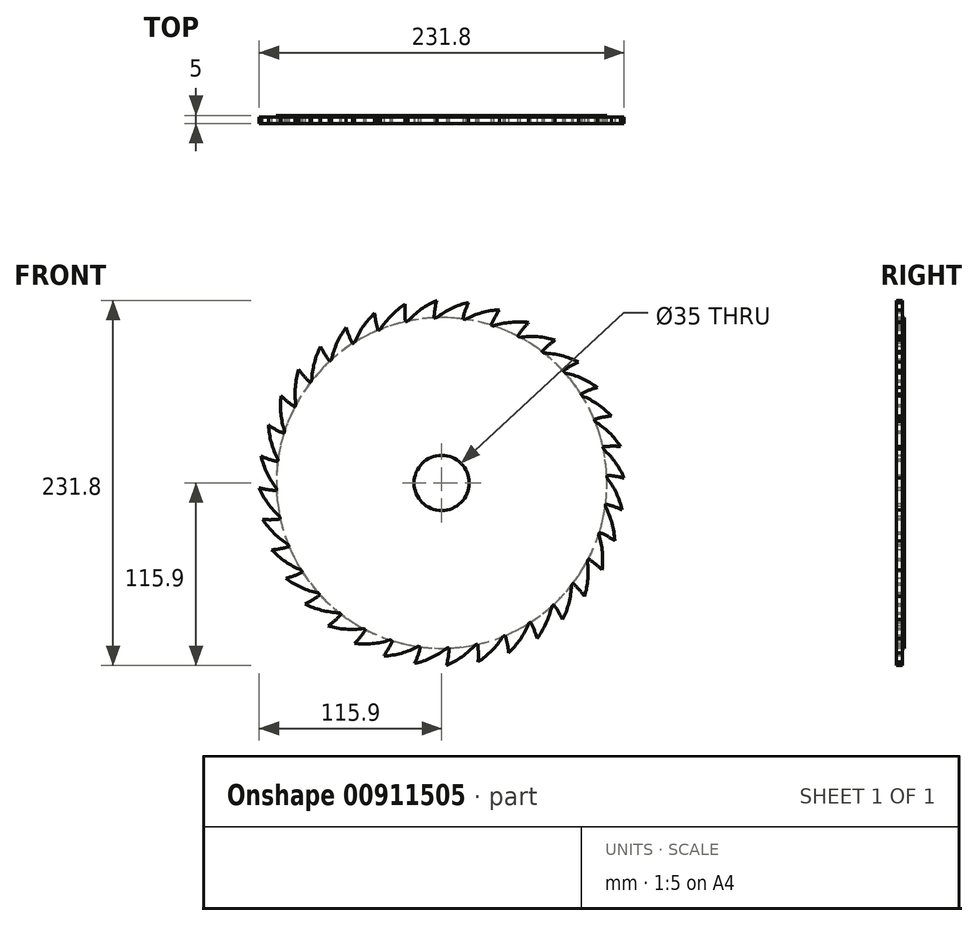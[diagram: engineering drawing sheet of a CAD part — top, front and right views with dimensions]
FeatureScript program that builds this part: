
annotation { "Feature Type Name" : "Feature", "Feature Type Description" : "" }
export const myFeature = defineFeature(function(context is Context, id is Id, definition is map)
    precondition{}
    {
        {
            var Q0;
            Q0=qCreatedBy(makeId("Front.planeOp"),FACE);
            var sketch = newSketch(context, id + "F0", { "sketchPlane" : qUnion([Q0])});
            skCircle(sketch, "E0", {"center": v(0, 0) * mm, "radius": 125 * mm});
            skCircle(sketch, "E1", {"center": v(0, 0) * mm, "radius": 105 * mm});
            skSolve(sketch);
        }
        {
            var Q0;
            Q0=makeQuery(id+"F0.imprint","IMPRINT",FACE,{"disambiguationData":[TD([[makeQuery(id+"F0.imprint","IMPRINT",EDGE,{"derivedFrom":sQuery(id+"F0.wireOp",EDGE,"E1")}),1.0]])]});
            extrude(context, id + "F1", {"entities" : qUnion([Q0]), "endBound" : BoundingType.SYMMETRIC, "depth" : 5 * mm, "offsetDistance" : 25 * mm});
        }
        {
            var Q0;
            Q0=makeQuery(id+"F1.opExtrude","CAP_FACE",FACE,{"disambiguationData":[OSD([sQuery(id+"F0.wireOp",EDGE,"E1")])],"isStart":false});
            var sketch = newSketch(context, id + "F2", { "sketchPlane" : qUnion([Q0])});
            skLineSegment(sketch, "E2", {"start": v(4.66, 77.54) * mm, "end": v(40.5, 61.1) * mm});
            skArc(sketch, "E3", {"start": v(55.27, 101.92) * mm, "mid": v(26.4, 97.15) * mm, "end": v(4.66, 77.54) * mm});
            skArc(sketch, "E4", {"start": v(55.27, 101.92) * mm, "mid": v(43.34, 83.16) * mm, "end": v(40.5, 61.1) * mm});
            skSolve(sketch);
        }
        {
            var Q0;
            {var subQ0=sQuery(id+"F2.wireOp",EDGE,"E4");var subQ1=sQuery(id+"F2.wireOp",EDGE,"E3");var subQ2=makeQuery(id+"F2.imprint","INTERSECT",VERTEX,{"derivedFrom":[subQ1,subQ0]});Q0=makeQuery(id+"F2.imprint","IMPRINT",FACE,{"disambiguationData":[TD([[makeQuery(id+"F2.imprint","IMPRINT",EDGE,{"disambiguationData":[TD([[subQ2,-1.0]])],"derivedFrom":subQ1}),1.0]])]});}
            var Q1;
            Q1=makeQuery(id+"F1.opExtrude","CAP_FACE",FACE,{"disambiguationData":[OSD([sQuery(id+"F0.wireOp",EDGE,"E1")])],"isStart":true});
            extrude(context, id + "F3", {"entities" : qUnion([Q0]), "operationType" : NewBodyOperationType.ADD, "oppositeDirection" : true, "depth" : 4 * mm, "endBoundEntityFace" : qUnion([Q1]), "offsetDistance" : 25 * mm});
        }
        {
            var Q0;
            Q0=makeQuery(id+"F1.opExtrude","SWEPT_BODY",BODY,{"disambiguationData":[OSD([sQuery(id+"F0.wireOp",EDGE,"E1")])]});
            var Q1;
            Q1=makeQuery(id+"F1.opExtrude","CAP_EDGE",EDGE,{"disambiguationData":[OSD([sQuery(id+"F0.wireOp",EDGE,"E1")])],"isStart":true});
            circularPattern(context, id + "F4", {"operationType" : NewBodyOperationType.ADD, "entities" : qUnion([Q0]), "axis" : qUnion([Q1]), "angle" : 360 * degree, "instanceCount" : 36, "equalSpace" : true});
        }
        {
            var Q0;
            {var subQ0=sQuery(id+"F0.wireOp",EDGE,"E1");Q0=makeQuery(id+"F4.opPattern","COPY",FACE,{"derivedFrom":makeQuery(id+"F3.boolean.opBoolean","MERGE",FACE,{"derivedFrom":[makeQuery(id+"F1.opExtrude","CAP_FACE",FACE,{"disambiguationData":[OSD([subQ0])],"isStart":false}),makeQuery(id+"F3.opExtrude","CAP_FACE",FACE,{"disambiguationData":[OSD([subQ0,sQuery(id+"F2.wireOp",EDGE,"E3"),sQuery(id+"F2.wireOp",EDGE,"E4")])],"isStart":true})]}),"instanceName":"5"});}
            var sketch = newSketch(context, id + "F5", { "sketchPlane" : qUnion([Q0])});
            skCircle(sketch, "E5", {"center": v(0, 0) * mm, "radius": 17.5 * mm});
            skSolve(sketch);
        }
        {
            var Q0;
            Q0=makeQuery(id+"F5.imprint","IMPRINT",FACE,{"disambiguationData":[TD([[makeQuery(id+"F5.imprint","IMPRINT",EDGE,{"derivedFrom":sQuery(id+"F5.wireOp",EDGE,"E5")}),1.0]])]});
            extrude(context, id + "F6", {"entities" : qUnion([Q0]), "operationType" : NewBodyOperationType.REMOVE, "endBound" : BoundingType.THROUGH_ALL, "oppositeDirection" : true, "depth" : 25 * mm, "offsetDistance" : 25 * mm});
        }
    });
